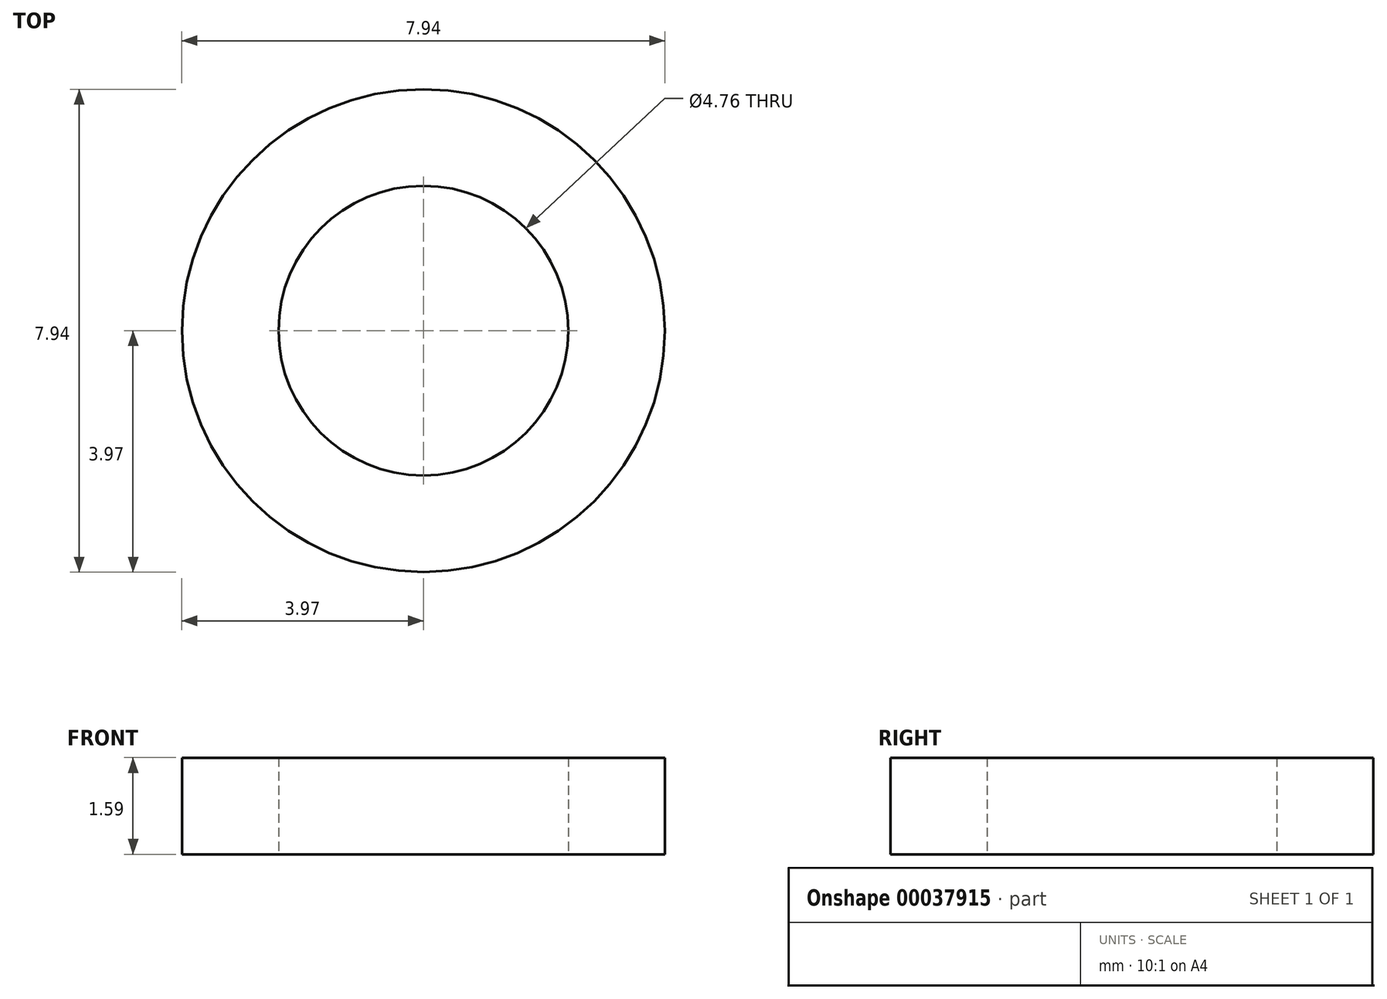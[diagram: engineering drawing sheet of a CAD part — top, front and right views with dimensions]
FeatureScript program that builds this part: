
annotation { "Feature Type Name" : "Feature", "Feature Type Description" : "" }
export const myFeature = defineFeature(function(context is Context, id is Id, definition is map)
    precondition{}
    {
        {
            var Q0;
            Q0=qCreatedBy(makeId("Top.planeOp"),FACE);
            var sketch = newSketch(context, id + "F0", { "sketchPlane" : qUnion([Q0])});
            skCircle(sketch, "E0", {"center": v(0, 0) * mm, "radius": 2.38 * mm});
            skCircle(sketch, "E1", {"center": v(0, 0) * mm, "radius": 3.97 * mm});
            skSolve(sketch);
        }
        {
            var Q0;
            Q0 = qSketchRegion(id + "F0", true);
            extrude(context, id + "F1", {"entities" : qUnion([Q0]), "depth" : 1.59 * mm});
        }
    });
